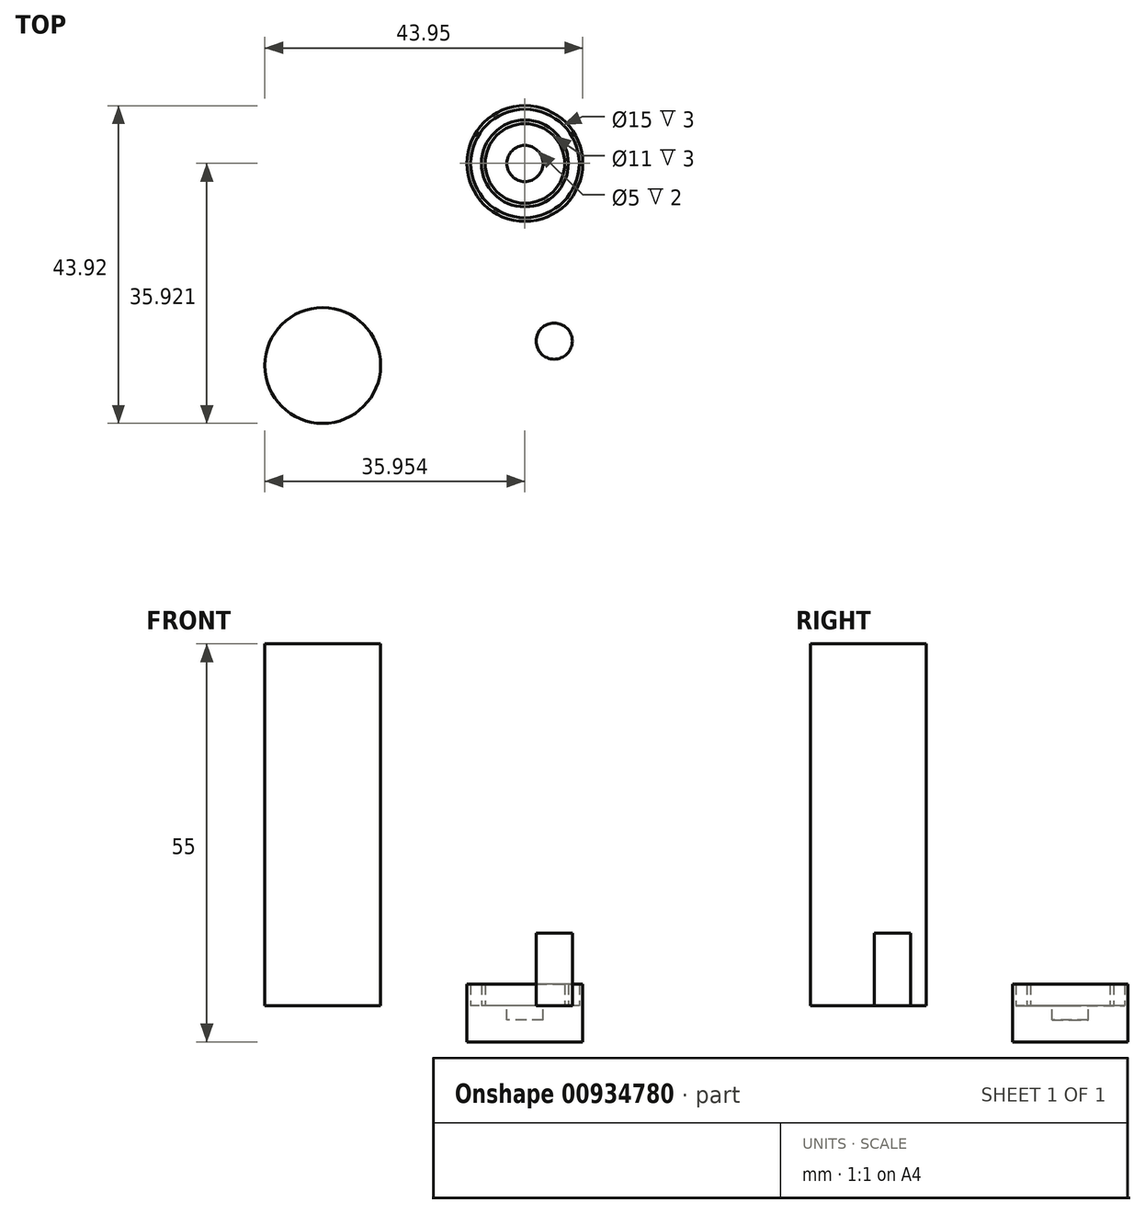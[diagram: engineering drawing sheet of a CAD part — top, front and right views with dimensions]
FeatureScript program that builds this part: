
annotation { "Feature Type Name" : "Feature", "Feature Type Description" : "" }
export const myFeature = defineFeature(function(context is Context, id is Id, definition is map)
    precondition{}
    {
        {
            var Q0;
            Q0=qCreatedBy(makeId("Top.planeOp"),FACE);
            var sketch = newSketch(context, id + "F0", { "sketchPlane" : qUnion([Q0])});
            skCircle(sketch, "E0", {"center": v(-46.44, 33) * mm, "radius": 8 * mm});
            skSolve(sketch);
        }
        {
            var Q0;
            Q0=makeQuery(id+"F0.imprint","IMPRINT",FACE,{"disambiguationData":[TD([[makeQuery(id+"F0.imprint","IMPRINT",EDGE,{"derivedFrom":sQuery(id+"F0.wireOp",EDGE,"E0")}),1.0]])]});
            extrude(context, id + "F1", {"entities" : qUnion([Q0]), "depth" : 50 * mm, "offsetDistance" : 25 * mm});
        }
        {
            var Q0;
            Q0=qCreatedBy(makeId("Top.planeOp"),FACE);
            var sketch = newSketch(context, id + "F2", { "sketchPlane" : qUnion([Q0])});
            skCircle(sketch, "E1", {"center": v(-18.49, 60.92) * mm, "radius": 8 * mm});
            skCircle(sketch, "E2.0", {"center": v(-18.49, 60.92) * mm, "radius": 7.5 * mm});
            skCircle(sketch, "E3.0", {"center": v(-18.49, 60.92) * mm, "radius": 6 * mm});
            skCircle(sketch, "E4.0", {"center": v(-18.49, 60.92) * mm, "radius": 5.5 * mm});
            skCircle(sketch, "E5", {"center": v(-18.49, 60.92) * mm, "radius": 2.5 * mm});
            skSolve(sketch);
        }
        {
            var Q0;
            Q0=makeQuery(id+"F2.imprint","IMPRINT",FACE,{"disambiguationData":[TD([[makeQuery(id+"F2.imprint","IMPRINT",EDGE,{"derivedFrom":sQuery(id+"F2.wireOp",EDGE,"E2.0")}),1.0]])]});
            var Q1;
            Q1=makeQuery(id+"F2.imprint","IMPRINT",FACE,{"disambiguationData":[TD([[makeQuery(id+"F2.imprint","IMPRINT",EDGE,{"derivedFrom":sQuery(id+"F2.wireOp",EDGE,"E3.0")}),1.0]])]});
            var Q2;
            Q2=makeQuery(id+"F2.imprint","IMPRINT",FACE,{"disambiguationData":[TD([[makeQuery(id+"F2.imprint","IMPRINT",EDGE,{"derivedFrom":sQuery(id+"F2.wireOp",EDGE,"E4.0")}),1.0]])]});
            var Q3;
            Q3=makeQuery(id+"F2.imprint","IMPRINT",FACE,{"disambiguationData":[TD([[makeQuery(id+"F2.imprint","IMPRINT",EDGE,{"derivedFrom":sQuery(id+"F2.wireOp",EDGE,"E1")}),1.0]])]});
            var Q4;
            Q4=makeQuery(id+"F2.imprint","IMPRINT",FACE,{"disambiguationData":[TD([[makeQuery(id+"F2.imprint","IMPRINT",EDGE,{"derivedFrom":sQuery(id+"F2.wireOp",EDGE,"E5")}),1.0]])]});
            extrude(context, id + "F3", {"entities" : qUnion([Q0, Q1, Q2, Q3, Q4]), "oppositeDirection" : true, "depth" : 5 * mm, "offsetDistance" : 25 * mm});
        }
        {
            var Q0;
            Q0=makeQuery(id+"F2.imprint","IMPRINT",FACE,{"disambiguationData":[TD([[makeQuery(id+"F2.imprint","IMPRINT",EDGE,{"derivedFrom":sQuery(id+"F2.wireOp",EDGE,"E1")}),1.0]])]});
            var Q1;
            Q1=makeQuery(id+"F2.imprint","IMPRINT",FACE,{"disambiguationData":[TD([[makeQuery(id+"F2.imprint","IMPRINT",EDGE,{"derivedFrom":sQuery(id+"F2.wireOp",EDGE,"E3.0")}),1.0]])]});
            extrude(context, id + "F4", {"entities" : qUnion([Q0, Q1]), "operationType" : NewBodyOperationType.ADD, "depth" : 3 * mm, "offsetDistance" : 25 * mm});
        }
        {
            var Q0;
            Q0=makeQuery(id+"F2.imprint","IMPRINT",FACE,{"disambiguationData":[TD([[makeQuery(id+"F2.imprint","IMPRINT",EDGE,{"derivedFrom":sQuery(id+"F2.wireOp",EDGE,"E5")}),1.0]])]});
            extrude(context, id + "F5", {"entities" : qUnion([Q0]), "operationType" : NewBodyOperationType.REMOVE, "oppositeDirection" : true, "depth" : 2 * mm, "offsetDistance" : 25 * mm});
        }
        {
            var Q0;
            Q0=qCreatedBy(makeId("Top.planeOp"),FACE);
            var sketch = newSketch(context, id + "F6", { "sketchPlane" : qUnion([Q0])});
            skCircle(sketch, "E6", {"center": v(-14.44, 36.37) * mm, "radius": 2.5 * mm});
            skSolve(sketch);
        }
        {
            var Q0;
            Q0=makeQuery(id+"F6.imprint","IMPRINT",FACE,{"disambiguationData":[TD([[makeQuery(id+"F6.imprint","IMPRINT",EDGE,{"derivedFrom":sQuery(id+"F6.wireOp",EDGE,"E6")}),1.0]])]});
            extrude(context, id + "F7", {"entities" : qUnion([Q0]), "depth" : 10 * mm, "offsetDistance" : 25 * mm});
        }
    });
